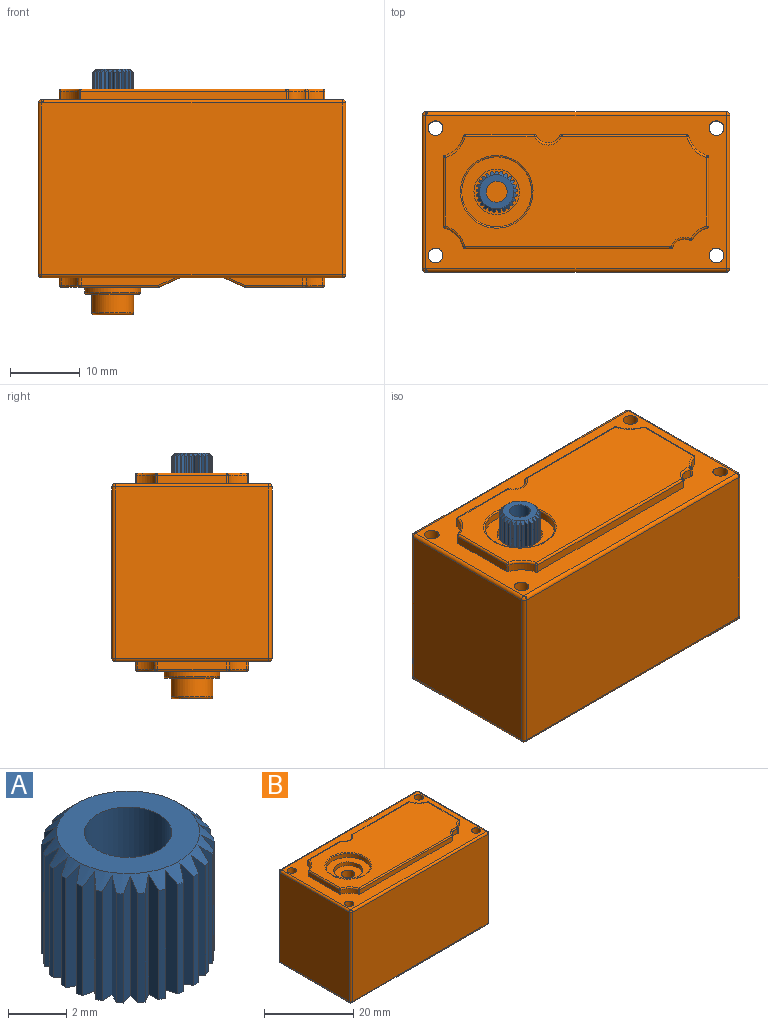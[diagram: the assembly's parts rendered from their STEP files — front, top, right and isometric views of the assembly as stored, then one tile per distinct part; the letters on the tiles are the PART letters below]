
ASSEMBLY  parts=2 mates=1
PART A: 79 faces, bbox 5.9x5.9x5.1 mm
  f0: cylinder r=2.96mm len=4.6mm, axis (0,0,-1), area 1.2mm2, adj f26,f27,f55,f76
  f1: cylinder r=2.96mm len=4.6mm, axis (0,0,-1), area 1.2mm2, adj f26,f27,f74,f77
  f2: cylinder r=2.96mm len=4.6mm, axis (0,0,-1), area 1.2mm2, adj f26,f27,f72,f75
  f3: cylinder r=2.96mm len=4.6mm, axis (0,0,-1), area 1.2mm2, adj f26,f27,f70,f73
  f4: cylinder r=2.96mm len=4.6mm, axis (0,0,-1), area 1.2mm2, adj f26,f27,f68,f71
  f5: cylinder r=2.96mm len=4.6mm, axis (0,0,-1), area 1.2mm2, adj f26,f27,f66,f69
  f6: cylinder r=2.96mm len=4.6mm, axis (0,0,-1), area 1.2mm2, adj f26,f27,f64,f67
  f7: cylinder r=2.96mm len=4.6mm, axis (0,0,-1), area 1.2mm2, adj f26,f27,f62,f65
  f8: cylinder r=2.96mm len=4.6mm, axis (0,0,-1), area 1.2mm2, adj f26,f27,f53,f60
  f9: cylinder r=2.96mm len=4.6mm, axis (0,0,-1), area 1.2mm2, adj f26,f27,f58,f61
  f10: cylinder r=2.96mm len=4.6mm, axis (0,0,-1), area 1.2mm2, adj f26,f27,f56,f59
  f11: cylinder r=2.96mm len=4.6mm, axis (0,0,-1), area 1.2mm2, adj f26,f27,f54,f57
  f12: cylinder r=2.96mm len=4.6mm, axis (0,0,-1), area 1.2mm2, adj f26,f27,f51,f52
  f13: cylinder r=2.96mm len=4.6mm, axis (0,0,-1), area 1.2mm2, adj f26,f27,f49,f50
  f14: cylinder r=2.96mm len=4.6mm, axis (0,0,-1), area 1.2mm2, adj f26,f27,f47,f48
  f15: cylinder r=2.96mm len=4.6mm, axis (0,0,-1), area 1.2mm2, adj f26,f27,f43,f46
  f16: cylinder r=2.96mm len=4.6mm, axis (0,0,-1), area 1.2mm2, adj f26,f27,f41,f44
  f17: cylinder r=2.96mm len=4.6mm, axis (0,0,-1), area 1.2mm2, adj f26,f27,f42,f45
  f18: cylinder r=2.96mm len=4.6mm, axis (0,0,-1), area 1.2mm2, adj f26,f27,f39,f40
  f19: cylinder r=2.96mm len=4.6mm, axis (0,0,-1), area 1.2mm2, adj f26,f27,f31,f38
  f20: cylinder r=2.96mm len=4.6mm, axis (0,0,-1), area 1.2mm2, adj f26,f27,f35,f36
  f21: cylinder r=2.96mm len=4.6mm, axis (0,0,-1), area 1.2mm2, adj f26,f27,f29,f34
  f22: cylinder r=2.96mm len=4.6mm, axis (0,0,-1), area 1.2mm2, adj f26,f27,f32,f37
  f23: cylinder r=2.96mm len=4.6mm, axis (0,0,-1), area 1.2mm2, adj f26,f27,f30,f33
  f24: cylinder r=2.96mm len=4.6mm, axis (0,0,-1), area 1.2mm2, adj f26,f27,f28,f63
  f25: plane 4.92x4.92mm, normal (0,0,1), area 11.9mm2, adj f27,f78
  f26: plane 5.92x5.91mm, normal (0,0,-1), area 17.8mm2, adj f0,f1,f2,f3,f4,f5,f6,f7
  f27: cone r=2.46mm half-angle=45deg, axis (0,0,-1), area 8.4mm2, adj f0,f1,f2,f3,f4,f5,f6,f7
  f28: plane 5.05x0.5mm, normal (-0.21,-0.98,0), area 2.4mm2, adj f24,f26,f27,f29
  f29: plane 5.05x0.38mm, normal (-0.74,0.67,0), area 2.4mm2, adj f21,f26,f27,f28
  f30: plane 5.05x0.37mm, normal (0.71,-0.7,0), area 2.4mm2, adj f23,f26,f27,f31
  f31: plane 5.05x0.49mm, normal (-0.96,-0.27,0), area 2.4mm2, adj f19,f26,f27,f30
  f32: plane 5.05x0.44mm, normal (0.52,-0.86,0), area 2.4mm2, adj f22,f26,f27,f33
  f33: plane 5.05x0.51mm, normal (-1,-0.02,0), area 2.4mm2, adj f23,f26,f27,f32
  f34: plane 5.05x0.51mm, normal (0.04,-1,0), area 2.4mm2, adj f21,f26,f27,f35
  f35: plane 5.05x0.45mm, normal (-0.89,0.46,0), area 2.4mm2, adj f20,f26,f27,f34
  f36: plane 5.05x0.49mm, normal (0.29,-0.96,0), area 2.4mm2, adj f20,f26,f27,f37
  f37: plane 5.05x0.5mm, normal (-0.97,0.23,0), area 2.4mm2, adj f22,f26,f27,f36
  f38: plane 5.05x0.44mm, normal (0.87,-0.5,0), area 2.4mm2, adj f19,f26,f27,f39
  f39: plane 5.05x0.44mm, normal (-0.87,-0.5,0), area 2.4mm2, adj f18,f26,f27,f38
  f40: plane 5.05x0.49mm, normal (0.96,-0.27,0), area 2.4mm2, adj f18,f26,f27,f41
  f41: plane 5.05x0.37mm, normal (-0.71,-0.7,0), area 2.4mm2, adj f16,f26,f27,f40
  f42: plane 5.05x0.5mm, normal (0.97,0.23,0), area 2.4mm2, adj f17,f26,f27,f43
  f43: plane 5.05x0.49mm, normal (-0.29,-0.96,0), area 2.4mm2, adj f15,f26,f27,f42
  f44: plane 5.05x0.51mm, normal (1,-0.02,0), area 2.4mm2, adj f16,f26,f27,f45
  f45: plane 5.05x0.44mm, normal (-0.52,-0.86,0), area 2.4mm2, adj f17,f26,f27,f44
  f46: plane 5.05x0.45mm, normal (0.89,0.46,0), area 2.4mm2, adj f15,f26,f27,f47
  f47: plane 5.05x0.51mm, normal (-0.04,-1,0), area 2.4mm2, adj f14,f26,f27,f46
  f48: plane 5.05x0.38mm, normal (0.74,0.67,0), area 2.4mm2, adj f14,f26,f27,f49
  f49: plane 5.05x0.5mm, normal (0.21,-0.98,0), area 2.4mm2, adj f13,f26,f27,f48
  f50: plane 5.05x0.43mm, normal (0.55,0.83,0), area 2.4mm2, adj f13,f26,f27,f51
  f51: plane 5.05x0.46mm, normal (0.44,-0.9,0), area 2.4mm2, adj f12,f26,f27,f50
  f52: plane 5.05x0.48mm, normal (0.33,0.94,0), area 2.4mm2, adj f12,f26,f27,f53
  f53: plane 5.05x0.39mm, normal (0.65,-0.76,0), area 2.4mm2, adj f8,f26,f27,f52
  f54: plane 5.05x0.4mm, normal (-0.62,0.78,0), area 2.4mm2, adj f11,f26,f27,f55
  f55: plane 5.05x0.5mm, normal (0.99,0.15,0), area 2.4mm2, adj f0,f26,f27,f54
  f56: plane 5.05x0.47mm, normal (-0.41,0.91,0), area 2.4mm2, adj f10,f26,f27,f57
  f57: plane 5.05x0.51mm, normal (0.99,-0.1,0), area 2.4mm2, adj f11,f26,f27,f56
  f58: plane 5.05x0.5mm, normal (-0.17,0.99,0), area 2.4mm2, adj f9,f26,f27,f59
  f59: plane 5.05x0.48mm, normal (0.94,-0.35,0), area 2.4mm2, adj f10,f26,f27,f58
  f60: plane 5.05x0.51mm, normal (0.08,1,0), area 2.4mm2, adj f8,f26,f27,f61
  f61: plane 5.05x0.42mm, normal (0.82,-0.57,0), area 2.4mm2, adj f9,f26,f27,f60
  f62: plane 5.05x0.46mm, normal (-0.44,-0.9,0), area 2.4mm2, adj f7,f26,f27,f63
  f63: plane 5.05x0.43mm, normal (-0.55,0.83,0), area 2.4mm2, adj f24,f26,f27,f62
  f64: plane 5.05x0.39mm, normal (-0.65,-0.76,0), area 2.4mm2, adj f6,f26,f27,f65
  f65: plane 5.05x0.48mm, normal (-0.33,0.94,0), area 2.4mm2, adj f7,f26,f27,f64
  f66: plane 5.05x0.42mm, normal (-0.82,-0.57,0), area 2.4mm2, adj f5,f26,f27,f67
  f67: plane 5.05x0.51mm, normal (-0.08,1,0), area 2.4mm2, adj f6,f26,f27,f66
  f68: plane 5.05x0.48mm, normal (-0.94,-0.35,0), area 2.4mm2, adj f4,f26,f27,f69
  f69: plane 5.05x0.5mm, normal (0.17,0.99,0), area 2.4mm2, adj f5,f26,f27,f68
  f70: plane 5.05x0.51mm, normal (-0.99,-0.1,0), area 2.4mm2, adj f3,f26,f27,f71
  f71: plane 5.05x0.47mm, normal (0.41,0.91,0), area 2.4mm2, adj f4,f26,f27,f70
  f72: plane 5.05x0.5mm, normal (-0.99,0.15,0), area 2.4mm2, adj f2,f26,f27,f73
  f73: plane 5.05x0.4mm, normal (0.62,0.78,0), area 2.4mm2, adj f3,f26,f27,f72
  f74: plane 5.05x0.47mm, normal (-0.92,0.39,0), area 2.4mm2, adj f1,f26,f27,f75
  f75: plane 5.05x0.41mm, normal (0.8,0.6,0), area 2.4mm2, adj f2,f26,f27,f74
  f76: plane 5.05x0.41mm, normal (-0.8,0.6,0), area 2.4mm2, adj f0,f26,f27,f77
  f77: plane 5.05x0.47mm, normal (0.92,0.39,0), area 2.4mm2, adj f1,f26,f27,f76
  f78: cylinder r=1.5mm len=5.1mm, axis (0,0,1), area 48.1mm2, adj f25,f26
PART B: 152 faces, bbox 44.3x24.1x32.6 mm
  f0: plane 43.02x21.92mm, normal (0,0,1), area 340mm2, adj f71,f72,f73,f74,f75,f76,f77,f78
  f1: plane 10.69x1.1mm, normal (0,-1,0), area 10.4mm2, adj f4,f16,f58,f60
  f2: plane 13.49x1.1mm, normal (0,-1,0), area 13.5mm2, adj f4,f22,f55,f57
  f3: plane 15.6x11.11mm, normal (0,0,-1), area 163.4mm2, adj f44,f60,f61,f62,f63,f64,f65,f66
  f4: plane 43.3x22.2mm, normal (0,0,-1), area 334.4mm2, adj f1,f2,f9,f10,f11,f12,f13,f14
  f5: plane 24.5x21.92mm, normal (-1,0,0), area 537.1mm2, adj f138,f139,f147,f148
  f6: plane 43.02x24.5mm, normal (0,-1,0), area 1054.1mm2, adj f140,f145,f148,f151
  f7: plane 24.5x21.92mm, normal (1,0,0), area 537.1mm2, adj f135,f136,f145,f146
  f8: plane 43.02x24.5mm, normal (0,1,0), area 1054.1mm2, adj f132,f136,f137,f138
  f9: plane 10.69x1.1mm, normal (0,1,0), area 10.4mm2, adj f4,f10,f68,f70
  f10: cylinder r=0.5mm len=1.1mm, axis (0,0,-1), area 0.7mm2, adj f4,f9,f11,f67
  f11: cylinder r=4mm len=2.41mm, axis (0,0,1), area 3.8mm2, adj f4,f10,f12,f66
  f12: cylinder r=0.5mm len=1.1mm, axis (0,0,-1), area 0.7mm2, adj f4,f11,f13,f65
  f13: plane 9.79x1.1mm, normal (1,0,0), area 10.8mm2, adj f4,f12,f14,f64
  f14: cylinder r=0.5mm len=1.1mm, axis (0,0,-1), area 0.7mm2, adj f4,f13,f15,f63
  f15: cylinder r=4mm len=2.41mm, axis (0,0,1), area 3.8mm2, adj f4,f14,f16,f62
  f16: cylinder r=0.5mm len=1.1mm, axis (0,0,-1), area 0.7mm2, adj f1,f4,f15,f61
  f17: plane 17.2x5mm, normal (-1,0,0), area 86mm2, adj f4,f18,f20,f21
  f18: plane 6x5mm, normal (0,-1,0), area 30mm2, adj f4,f17,f19,f21
  f19: plane 17.2x5mm, normal (1,0,0), area 86mm2, adj f4,f18,f20,f21
  f20: plane 6x5mm, normal (0,1,0), area 30mm2, adj f4,f17,f19,f21
  f21: plane 17.2x6mm, normal (0,0,-1), area 103.2mm2, adj f17,f18,f19,f20
  f22: cylinder r=0.5mm len=1.1mm, axis (0,0,-1), area 0.7mm2, adj f2,f4,f23,f54
  f23: cylinder r=4mm len=2.41mm, axis (0,0,1), area 3.8mm2, adj f4,f22,f24,f53
  f24: cylinder r=0.5mm len=1.1mm, axis (0,0,-1), area 0.7mm2, adj f4,f23,f25,f52
  f25: plane 9.79x1.1mm, normal (-1,0,0), area 10.8mm2, adj f4,f24,f26,f51
  f26: cylinder r=0.5mm len=1.1mm, axis (0,0,-1), area 0.7mm2, adj f4,f25,f27,f50
  f27: cylinder r=4mm len=2.41mm, axis (0,0,1), area 3.8mm2, adj f4,f26,f28,f49
  f28: cylinder r=0.5mm len=1.1mm, axis (0,0,-1), area 0.7mm2, adj f4,f27,f29,f48
  f29: plane 13.49x1.1mm, normal (0,1,0), area 13.5mm2, adj f4,f28,f45,f47
  f30: plane 15.6x13.91mm, normal (0,0,-1), area 156.9mm2, adj f31,f42,f47,f48,f49,f50,f51,f52
  f31: cylinder r=4mm len=8mm, axis (0,0,1), area 17.6mm2, adj f30,f39
  f32: plane 7.4x7.4mm, normal (0,0,-1), area 14.7mm2, adj f33,f39
  f33: cylinder r=3mm len=6mm, axis (0,0,1), area 49mm2, adj f32,f37
  f34: plane 5.4x5.4mm, normal (0,0,-1), area 17.6mm2, adj f37,f38
  f35: cylinder r=1mm len=4.2mm, axis (0,0,-1), area 26.4mm2, adj f36,f38
  f36: plane 2x2mm, normal (0,0,-1), area 3.1mm2, adj f35
  f37: torus R=2.7mm, axis (0,0,-1), area 8.6mm2, adj f33,f34
  f38: cone r=1mm half-angle=45deg, axis (0,0,-1), area 3.1mm2, adj f34,f35
  f39: torus R=3.7mm, axis (0,0,-1), area 11.5mm2, adj f31,f32
  f40: plane 15.6x2.81mm, normal (0.41,0,-0.91), area 48.1mm2, adj f41,f42,f45,f57
  f41: plane 16.04x0.12mm, normal (1,0,-0.05), area 1.5mm2, adj f4,f40,f45,f57
  f42: cylinder r=0.3mm len=15.6mm, axis (0,-1,0), area 2mm2, adj f30,f40,f46,f56
  f43: plane 15.6x3.02mm, normal (-0.41,0,-0.91), area 51.7mm2, adj f4,f44,f58,f70
  f44: cylinder r=0.3mm len=15.6mm, axis (0,1,0), area 2mm2, adj f3,f43,f59,f69
  f45: cylinder r=0.3mm len=2.97mm, axis (-0.91,0,-0.41), area 1.4mm2, adj f4,f29,f40,f41,f46
  f46: sphere r=0.3mm, area 0mm2, adj f42,f45,f47
  f47: cylinder r=0.3mm len=11.07mm, axis (-1,0,0), area 5.2mm2, adj f29,f30,f46,f48
  f48: bspline ~0.63x0.55mm, area 0.2mm2, adj f28,f30,f47,f49
  f49: torus R=4.3mm, axis (0,0,-1), area 1.7mm2, adj f27,f30,f48,f50
  f50: bspline ~0.56x0.54mm, area 0.2mm2, adj f26,f30,f49,f51
  f51: cylinder r=0.3mm len=9.79mm, axis (0,-1,0), area 4.6mm2, adj f25,f30,f50,f52
  f52: bspline ~0.6x0.46mm, area 0.2mm2, adj f24,f30,f51,f53
  f53: torus R=4.3mm, axis (0,0,-1), area 1.7mm2, adj f23,f30,f52,f54
  f54: bspline ~0.56x0.55mm, area 0.2mm2, adj f22,f30,f53,f55
  f55: cylinder r=0.3mm len=11.07mm, axis (1,0,0), area 5.2mm2, adj f2,f30,f54,f56
  f56: sphere r=0.3mm, area 0mm2, adj f42,f55,f57
  f57: cylinder r=0.3mm len=2.97mm, axis (-0.91,0,-0.41), area 1.4mm2, adj f2,f4,f40,f41,f56
  f58: cylinder r=0.3mm len=3.14mm, axis (-0.91,0,0.41), area 1.4mm2, adj f1,f4,f43,f59
  f59: sphere r=0.3mm, area 0mm2, adj f44,f58,f60
  f60: cylinder r=0.3mm len=8.27mm, axis (1,0,0), area 3.9mm2, adj f1,f3,f59,f61
  f61: bspline ~0.61x0.46mm, area 0.2mm2, adj f3,f16,f60,f62
  f62: bspline ~7.53x4.84mm, area 1.7mm2, adj f3,f15,f61,f63
  f63: bspline ~0.56x0.54mm, area 0.2mm2, adj f3,f14,f62,f64
  f64: cylinder r=0.3mm len=9.79mm, axis (0,1,0), area 4.6mm2, adj f3,f13,f63,f65
  f65: bspline ~0.6x0.46mm, area 0.2mm2, adj f3,f12,f64,f66
  f66: bspline ~3.32x2.97mm, area 1.7mm2, adj f3,f11,f65,f67
  f67: bspline ~0.56x0.55mm, area 0.2mm2, adj f3,f10,f66,f68
  f68: cylinder r=0.3mm len=8.27mm, axis (-1,0,0), area 3.9mm2, adj f3,f9,f67,f69
  f69: sphere r=0.3mm, area 0mm2, adj f44,f68,f70
  f70: cylinder r=0.3mm len=3.14mm, axis (-0.91,0,0.41), area 1.4mm2, adj f4,f9,f43,f69
  f71: cylinder r=0.25mm len=1.2mm, axis (0,0,-1), area 0.4mm2, adj f0,f72,f93,f114
  f72: plane 9.88x1.2mm, normal (1,0,0), area 11.9mm2, adj f0,f71,f73,f116
  f73: cylinder r=0.25mm len=1.2mm, axis (0,0,-1), area 0.4mm2, adj f0,f72,f74,f118
  f74: cylinder r=4mm len=2.79mm, axis (0,0,-1), area 4.9mm2, adj f0,f73,f75,f120
  f75: cylinder r=0.25mm len=1.2mm, axis (0,0,-1), area 0.4mm2, adj f0,f74,f76,f122
  f76: plane 18.02x1.2mm, normal (0,1,0), area 21.6mm2, adj f0,f75,f77,f124,f126
  f77: cylinder r=0.3mm len=1.2mm, axis (0,0,1), area 0.4mm2, adj f0,f76,f78,f125
  f78: cylinder r=1.8mm len=3.21mm, axis (0,0,-1), area 4.8mm2, adj f0,f77,f79,f123
  f79: cylinder r=0.3mm len=1.2mm, axis (0,0,1), area 0.4mm2, adj f0,f78,f80,f121
  f80: plane 10.02x1.2mm, normal (0,1,0), area 12mm2, adj f0,f79,f81,f117,f119
  f81: cylinder r=0.25mm len=1.2mm, axis (0,0,-1), area 0.4mm2, adj f0,f80,f82,f115
  f82: cylinder r=4mm len=2.79mm, axis (0,0,-1), area 4.9mm2, adj f0,f81,f83,f113
  f83: cylinder r=0.25mm len=1.2mm, axis (0,0,1), area 0.4mm2, adj f0,f82,f84,f111
  f84: plane 9.88x1.2mm, normal (-1,0,0), area 11.9mm2, adj f0,f83,f85,f109
  f85: cylinder r=0.25mm len=1.2mm, axis (0,0,-1), area 0.4mm2, adj f0,f84,f86,f107
  f86: cylinder r=4mm len=2.79mm, axis (0,0,-1), area 4.9mm2, adj f0,f85,f87,f105
  f87: cylinder r=0.25mm len=1.2mm, axis (0,0,-1), area 0.4mm2, adj f0,f86,f88,f103
  f88: plane 29.43x1.2mm, normal (0,-1,0), area 35.3mm2, adj f0,f87,f89,f101,f102
  f89: cylinder r=0.3mm len=1.2mm, axis (0,0,1), area 0.4mm2, adj f0,f88,f90,f104
  f90: cylinder r=1.8mm len=2.43mm, axis (0,0,-1), area 3.5mm2, adj f0,f89,f91,f106
  f91: cylinder r=0.3mm len=1.2mm, axis (0,0,1), area 0.5mm2, adj f0,f90,f92,f108
  f92: plane 1.2x0.02mm, normal (0.84,-0.54,0), area 0mm2, adj f0,f91,f93,f110
  f93: cylinder r=4mm len=2.19mm, axis (0,0,-1), area 3.4mm2, adj f0,f71,f92,f112
  f94: plane 37.4x15.7mm, normal (0,0,1), area 473.9mm2, adj f101,f102,f105,f106,f109,f110,f112,f113
  f95: cylinder r=5mm len=10mm, axis (0,0,1), area 33mm2, adj f96,f127
  f96: plane 10x10mm, normal (0,0,1), area 45.4mm2, adj f95,f97
  f97: cylinder r=3.25mm len=6.5mm, axis (0,0,1), area 21mm2, adj f96,f98
  f98: plane 6.5x6.5mm, normal (0,0,1), area 26.1mm2, adj f97,f99
  f99: cylinder r=1.5mm len=3mm, axis (0,0,1), area 24.5mm2, adj f98,f100
  f100: plane 3x3mm, normal (0,0,1), area 7.1mm2, adj f99
  f101: cylinder r=0.3mm len=29.34mm, axis (-1,0,0), area 13.8mm2, adj f88,f94,f102,f103
  f102: cylinder r=0.3mm len=0.3mm, axis (-1,0,0), area 0mm2, adj f88,f94,f101,f104
  f103: bspline ~0.38x0.3mm, area 0.1mm2, adj f87,f101,f105
  f104: sphere r=0.3mm, area 0.1mm2, adj f89,f102,f106
  f105: torus R=4.3mm, axis (0,0,1), area 1.9mm2, adj f86,f94,f103,f107
  f106: torus R=2.1mm, axis (0,0,1), area 1.5mm2, adj f90,f94,f104,f108
  f107: bspline ~0.38x0.3mm, area 0.1mm2, adj f85,f105,f109
  f108: sphere r=0.3mm, area 0.2mm2, adj f91,f106,f110
  f109: cylinder r=0.3mm len=9.88mm, axis (0,1,0), area 4.6mm2, adj f84,f94,f107,f111
  f110: cylinder r=0.3mm len=0.3mm, axis (-0.54,-0.84,0), area 0mm2, adj f92,f94,f108,f112
  f111: bspline ~0.38x0.3mm, area 0.1mm2, adj f83,f109,f113
  f112: torus R=4.3mm, axis (0,0,1), area 1.3mm2, adj f93,f94,f110,f114
  f113: torus R=4.3mm, axis (0,0,1), area 1.9mm2, adj f82,f94,f111,f115
  f114: bspline ~0.38x0.3mm, area 0.1mm2, adj f71,f112,f116
  f115: bspline ~0.38x0.3mm, area 0.1mm2, adj f81,f113,f117
  f116: cylinder r=0.3mm len=9.88mm, axis (0,-1,0), area 4.6mm2, adj f72,f94,f114,f118
  f117: cylinder r=0.3mm len=9.9mm, axis (1,0,0), area 4.7mm2, adj f80,f94,f115,f119
  f118: bspline ~0.38x0.3mm, area 0.1mm2, adj f73,f116,f120
  f119: cylinder r=0.3mm len=0.3mm, axis (1,0,0), area 0.1mm2, adj f80,f94,f117,f121
  f120: torus R=4.3mm, axis (0,0,1), area 1.9mm2, adj f74,f94,f118,f122
  f121: sphere r=0.3mm, area 0.1mm2, adj f79,f119,f123
  f122: bspline ~0.38x0.3mm, area 0.1mm2, adj f75,f120,f124
  f123: torus R=2.1mm, axis (0,0,1), area 2mm2, adj f78,f94,f121,f125
  f124: cylinder r=0.3mm len=17.9mm, axis (1,0,0), area 8.4mm2, adj f76,f94,f122,f126
  f125: sphere r=0.3mm, area 0.1mm2, adj f77,f123,f126
  f126: cylinder r=0.3mm len=0.3mm, axis (1,0,0), area 0.1mm2, adj f76,f94,f124,f125
  f127: torus R=5.2mm, axis (0,0,1), area 10mm2, adj f94,f95
  f128: cylinder r=1.05mm len=25.5mm, axis (0,0,-1), area 168.2mm2, adj f0,f4
  f129: cylinder r=1.05mm len=25.5mm, axis (0,0,-1), area 168.2mm2, adj f0,f4
  f130: cylinder r=1.05mm len=25.5mm, axis (0,0,-1), area 168.2mm2, adj f0,f4
  f131: cylinder r=1.05mm len=25.5mm, axis (0,0,-1), area 168.2mm2, adj f0,f4
  f132: cylinder r=0.5mm len=43.02mm, axis (-1,0,0), area 33.8mm2, adj f0,f8,f133,f134
  f133: sphere r=0.5mm, area 0.2mm2, adj f132,f135,f136
  f134: sphere r=0.5mm, area 0.5mm2, adj f132,f138,f139
  f135: cylinder r=0.5mm len=21.92mm, axis (0,1,0), area 17.2mm2, adj f0,f7,f133,f141
  f136: cylinder r=0.5mm len=24.5mm, axis (0,0,-1), area 19.2mm2, adj f7,f8,f133,f142
  f137: cylinder r=0.5mm len=43.02mm, axis (1,0,0), area 33.8mm2, adj f4,f8,f142,f143
  f138: cylinder r=0.5mm len=24.5mm, axis (0,0,-1), area 19.2mm2, adj f5,f8,f134,f143
  f139: cylinder r=0.5mm len=21.92mm, axis (0,-1,0), area 17.2mm2, adj f0,f5,f134,f144
  f140: cylinder r=0.5mm len=43.02mm, axis (1,0,0), area 33.8mm2, adj f0,f6,f141,f144
  f141: sphere r=0.5mm, area 0.2mm2, adj f135,f140,f145
  f142: sphere r=0.5mm, area 0.4mm2, adj f136,f137,f146
  f143: sphere r=0.5mm, area 0.4mm2, adj f137,f138,f147
  f144: sphere r=0.5mm, area 0.5mm2, adj f139,f140,f148
  f145: cylinder r=0.5mm len=24.5mm, axis (0,0,-1), area 19.2mm2, adj f6,f7,f141,f149
  f146: cylinder r=0.5mm len=21.92mm, axis (0,-1,0), area 17.2mm2, adj f4,f7,f142,f149
  f147: cylinder r=0.5mm len=21.92mm, axis (0,1,0), area 17.2mm2, adj f4,f5,f143,f150
  f148: cylinder r=0.5mm len=24.5mm, axis (0,0,-1), area 19.2mm2, adj f5,f6,f144,f150
  f149: sphere r=0.5mm, area 0.4mm2, adj f145,f146,f151
  f150: sphere r=0.5mm, area 0.4mm2, adj f147,f148,f151
  f151: cylinder r=0.5mm len=43.02mm, axis (-1,0,0), area 33.8mm2, adj f4,f6,f149,f150
PLACE A t=(0.58,-0.91,-1.38)mm
PLACE B t=(0.58,-0.91,-1.38)mm fixed
MATE fastened A.f0 <-> B.f31  axis (0,0,-1) through (-10.77,-0.91,10.6)mm
